# Revit family: QF_COMCATER ALL BRANDS_RCT6-2-3G
name_source: partatom
category: Specialty Equipment
revit_build: Autodesk Revit 2014 (Build: 20140709_2115(x64)
units: mm (PartAtom-declared; Revit-internal decimal feet)

## types (2) — shared parameters
Accessory = No
Assembly Code = E1090320
BTUH = 15400 W
Depth Actual = 803 mm  [stored 2.63451 ft]
Description = 2 BURNER COMBINATION MODULAR TOP
Gas Flow = 0.0 L/s
Gas Size = 19 mm
Gas Size Flexible = 0 mm
Gas power kW = 15.4
Height Actual = 455 mm  [stored 1.49278 ft]
Length Actual = 600 mm
Manufacturer = TRUEHEAT
Model = RCT6-2-3G
Nominal Gas power = 15400 W
Type Comments = The Australian owned and designed* Trueheat RC Series of Gas Cooking Equipment has been developed for the restaurant and cafe market with a high quality finish, designed to fulfill the busy demands within a commercial kitchen.
Powerful 24MJ/hr open burners with individual standing pilots included.
100% Flame failure controls included as standard. Matt finish Euro look cast iron trivets radiate heat and design makes it easy to move pots around the surface.
16mm thick steel griddle plate with 22.5MJ/hr burner per 300mm section.
Note: Griddle is convertible to left hand side. Additional charges apply.

## type names (no varying parameters)
- RCT6-2-3G_Natural Gas
- RCT6-2-3G_LPG

note: [stored X ft] marks values corroborated as IEEE doubles in the binary element streams (Revit-internal decimal feet)

## geometry (parser evidence)
native form markers: Sweep x5
no freeform markers — native parametric forms only
